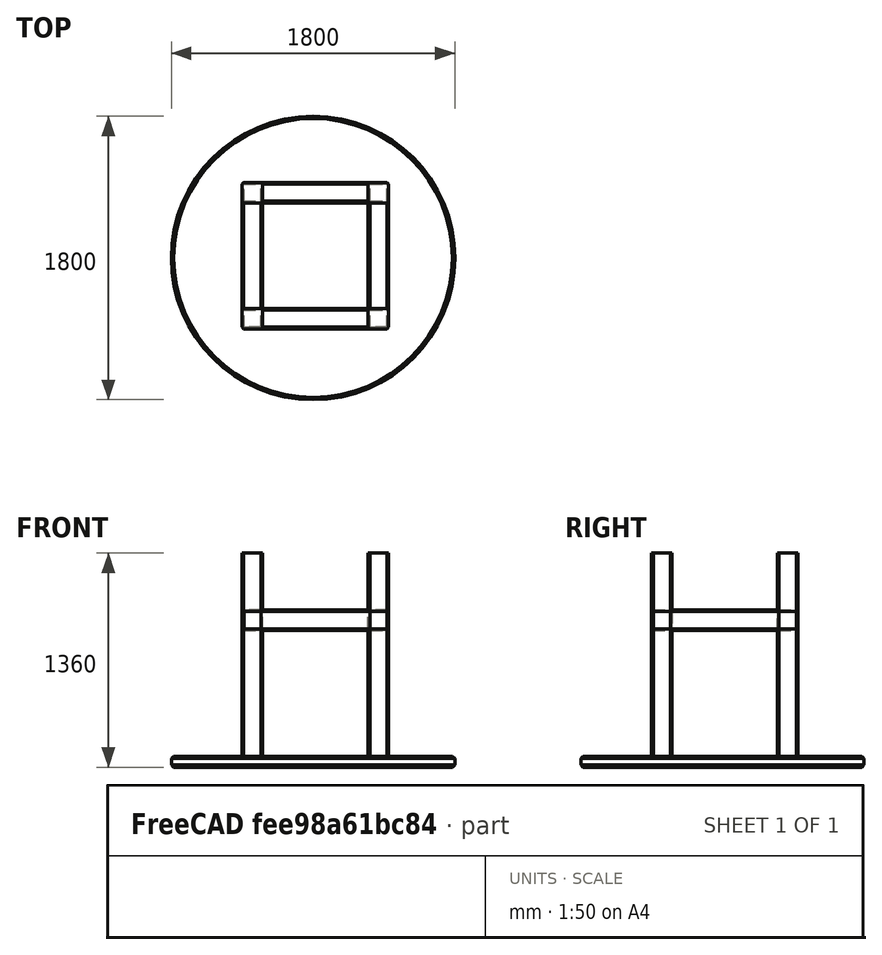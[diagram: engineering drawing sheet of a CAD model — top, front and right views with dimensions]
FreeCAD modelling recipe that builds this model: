
FCSTD DOCUMENT  (FreeCAD 1.0R38806 (Git))
Label: Mesa compleja biselada
License: All rights reserved
LicenseURL: http://en.wikipedia.org/wiki/All_rights_reserved
objects: Part::Chamfer×9, Part::Box×8, Part::Cylinder×1
note: 18 computed .brp shape members not serialized (recipe doc carries the construction recipe); baked Part::Feature solids carry a one-line shape summary decoded from their .brp

FEATURE [Part::Cylinder] Cylinder  label="Tablero"
  Angle = 360
  AttacherType = Attacher::AttachEngine3D
  FirstAngle = 0
  Height = 70
  Placement = pos=(-50,-50,0) rot=(0,0,1;0rad)
  Radius = 900
  SecondAngle = 0
FEATURE [Part::Box] Box  label="Pata1"
  AttacherType = Attacher::AttachEngine3D
  Height = 1300
  Length = 130
  Placement = pos=(-501,-500,60) rot=(0,0,1;0rad)
  Width = 130
FEATURE [Part::Box] Box001  label="Pata2"
  AttacherType = Attacher::AttachEngine3D
  Height = 1300
  Length = 130
  Placement = pos=(300,-500,60) rot=(0,0,1;0rad)
  Width = 130
FEATURE [Part::Box] Box002  label="Pata3"
  AttacherType = Attacher::AttachEngine3D
  Height = 1300
  Length = 130
  Placement = pos=(300,300,60) rot=(0,0,1;0rad)
  Width = 130
FEATURE [Part::Box] Box003  label="Pata4"
  AttacherType = Attacher::AttachEngine3D
  Height = 1300
  Length = 130
  Placement = pos=(-500,300,60) rot=(0,0,1;0rad)
  Width = 130
FEATURE [Part::Box] Box004  label="Union Pata1"
  AttacherType = Attacher::AttachEngine3D
  Height = 930
  Length = 130
  Placement = pos=(-500,300,1000) rot=(0,1,0;1.5708rad)
  Width = 130
FEATURE [Part::Box] Box005  label="Union Pata2"
  AttacherType = Attacher::AttachEngine3D
  Height = 930
  Length = 130
  Placement = pos=(-500,-500,1000) rot=(0,1,0;1.5708rad)
  Width = 130
FEATURE [Part::Box] Box006  label="Union Pata3"
  AttacherType = Attacher::AttachEngine3D
  Height = 930
  Length = 130
  Placement = pos=(-371,-500,870) rot=(0,1,1;3.14159rad)
  Width = 130
FEATURE [Part::Box] Box007  label="Union Pata4"
  AttacherType = Attacher::AttachEngine3D
  Height = 930
  Length = 130
  Placement = pos=(430,-500,870) rot=(0,1,1;3.14159rad)
  Width = 130
FEATURE [Part::Chamfer] Chamfer
  Base = -> Cylinder
  EdgeLinks = -> Cylinder [Edge2,Edge3]
  Edges = 2 edges r=15: [Edge2,Edge3]
FEATURE [Part::Chamfer] Chamfer001
  Base = -> Box
  EdgeLinks = -> Box [Edge1,Edge3,Edge5,Edge7]
  Edges = 4 edges r=10: [Edge1,Edge3,Edge5,Edge7]
FEATURE [Part::Chamfer] Chamfer002
  Base = -> Box001
  EdgeLinks = -> Box001 [Edge1,Edge3,Edge5,Edge7]
  Edges = 4 edges r=10: [Edge1,Edge3,Edge5,Edge7]
FEATURE [Part::Chamfer] Chamfer003
  Base = -> Box002
  EdgeLinks = -> Box002 [Edge1,Edge3,Edge5,Edge7]
  Edges = 4 edges r=10: [Edge1,Edge3,Edge5,Edge7]
FEATURE [Part::Chamfer] Chamfer004
  Base = -> Box003
  EdgeLinks = -> Box003 [Edge1,Edge3,Edge5,Edge7]
  Edges = 4 edges r=10: [Edge1,Edge3,Edge5,Edge7]
FEATURE [Part::Chamfer] Chamfer005
  Base = -> Box004
  EdgeLinks = -> Box004 [Edge1,Edge2,Edge3,Edge4,Edge5,Edge6,Edge7,Edge8,Edge9,Edge10,Edge11,Edge12]
  Edges = 12 edges r=10: [Edge1,Edge2,Edge3,Edge4,Edge5,Edge6,Edge7,Edge8,Edge9,Edge10,Edge11,Edge12]
FEATURE [Part::Chamfer] Chamfer006
  Base = -> Box005
  EdgeLinks = -> Box005 [Edge1,Edge2,Edge3,Edge4,Edge5,Edge6,Edge7,Edge8,Edge9,Edge10,Edge11,Edge12]
  Edges = 12 edges r=10: [Edge1,Edge2,Edge3,Edge4,Edge5,Edge6,Edge7,Edge8,Edge9,Edge10,Edge11,Edge12]
FEATURE [Part::Chamfer] Chamfer007
  Base = -> Box006
  EdgeLinks = -> Box006 [Edge1,Edge2,Edge3,Edge4,Edge5,Edge6,Edge7,Edge8,Edge9,Edge10,Edge11,Edge12]
  Edges = 12 edges r=10: [Edge1,Edge2,Edge3,Edge4,Edge5,Edge6,Edge7,Edge8,Edge9,Edge10,Edge11,Edge12]
FEATURE [Part::Chamfer] Chamfer008
  Base = -> Box007
  EdgeLinks = -> Box007 [Edge1,Edge2,Edge3,Edge4,Edge5,Edge6,Edge7,Edge8,Edge9,Edge10,Edge11,Edge12]
  Edges = 12 edges r=10: [Edge1,Edge2,Edge3,Edge4,Edge5,Edge6,Edge7,Edge8,Edge9,Edge10,Edge11,Edge12]
